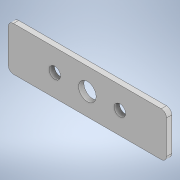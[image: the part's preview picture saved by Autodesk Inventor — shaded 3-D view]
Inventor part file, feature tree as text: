
AUTODESK INVENTOR PART (.ipt)
format: ipt  version: 2020 (Build 240168000, 168)  size: 119,808 bytes
history: native  units: mm
features: extrude x2, sketch x2, fillet x1
ambient origin geometry x8: Origin, YZ Plane, XZ Plane, XY Plane, X Axis, Y Axis, Z Axis, Center Point
bodies: Solid1 (feature_tree)
feature tree (5):
  extrude  "Extrusion1"  Depth=25.0mm
  fillet  "Fillet1"  Radius=37.0mm
  extrude  "Extrusion2"  Depth=10.0mm
  sketch  "Sketch1"  dims[d0=90.0mm d1=25.0mm d2=37.0mm]
  sketch  "Sketch2"  dims[d3=18.5mm d4=6.5mm d5=6.5mm d6=3.0mm d7=0.0mm d8=12.5mm d9=12.5mm d10=3.0mm d11=10.0mm d12=10.0mm d13=0.0mm]
